# Revit family: LBLE4_SERIE IRON LEGO 04
name_source: partatom
category: Luminarias
units: mm (PartAtom-declared; Revit-internal decimal feet)

## family parameters
Compartido = No
Corte con vacíos al cargar = No
Cota de conector redondo = Diámetro de uso
Origen de luz = Sí
Punto de cálculo de habitación = No
Se basa en plano de trabajo = Sí
Siempre vertical = Sí
Tipo de pieza = Normal

## types (1)
- IRON LEGO 04_LBLE4 W7W24BCN1F3RG
    Ancho = 65 mm
    Cambio de temperatura de color de luz atenuada = <Ninguno>
    Comentarios de vataje = 100-240V
    Descripción = LUMINARIA TIPO CIRCULAR CON UN CORTE EXTERNO DE 55MM DE DIAMETRO , PARA EMPOTRAR EN TECHO CON INSTALACION ESTANDAR CON 65MM DE DIAMETRO POR 75MM DE HOUSING, CUERPO Y ANILLO EN COLOR BLANCO , IP 20 USO PARA INTERIORES, CUENTA CON 1 LED TIPO OSRAM CON UNA POTENCIA TOTAL DE 7W, A UNA TEMPERATURA EN BLANCO CALIDO 3000K, IRC 90, APERTURA A 24 GRADOS, CON LENTE PARA UNA LUZ SUAVE, ALIMENTADA A 100-240V.
    Elevación por defecto = 1219 mm
    Fabricante = BRILLANT
    Filtro de color = 16777215
    Longitud de símbolo de origen de luz = 500 mm  [stored 1.64042 ft]
    Lámpara = Osram
    Modelo = LBLE4 W7W24BCN1F3RG
    Watt per fixture = 7
    Ángulo de campo de foco = 24.00°
    Ángulo de enfoque = 24.00°
    Ángulo de inclinación = 60.00°

note: [stored X ft] marks values corroborated as IEEE doubles in the binary element streams (Revit-internal decimal feet)

## geometry (parser evidence)
native form markers: Blend x2
no freeform markers — native parametric forms only
